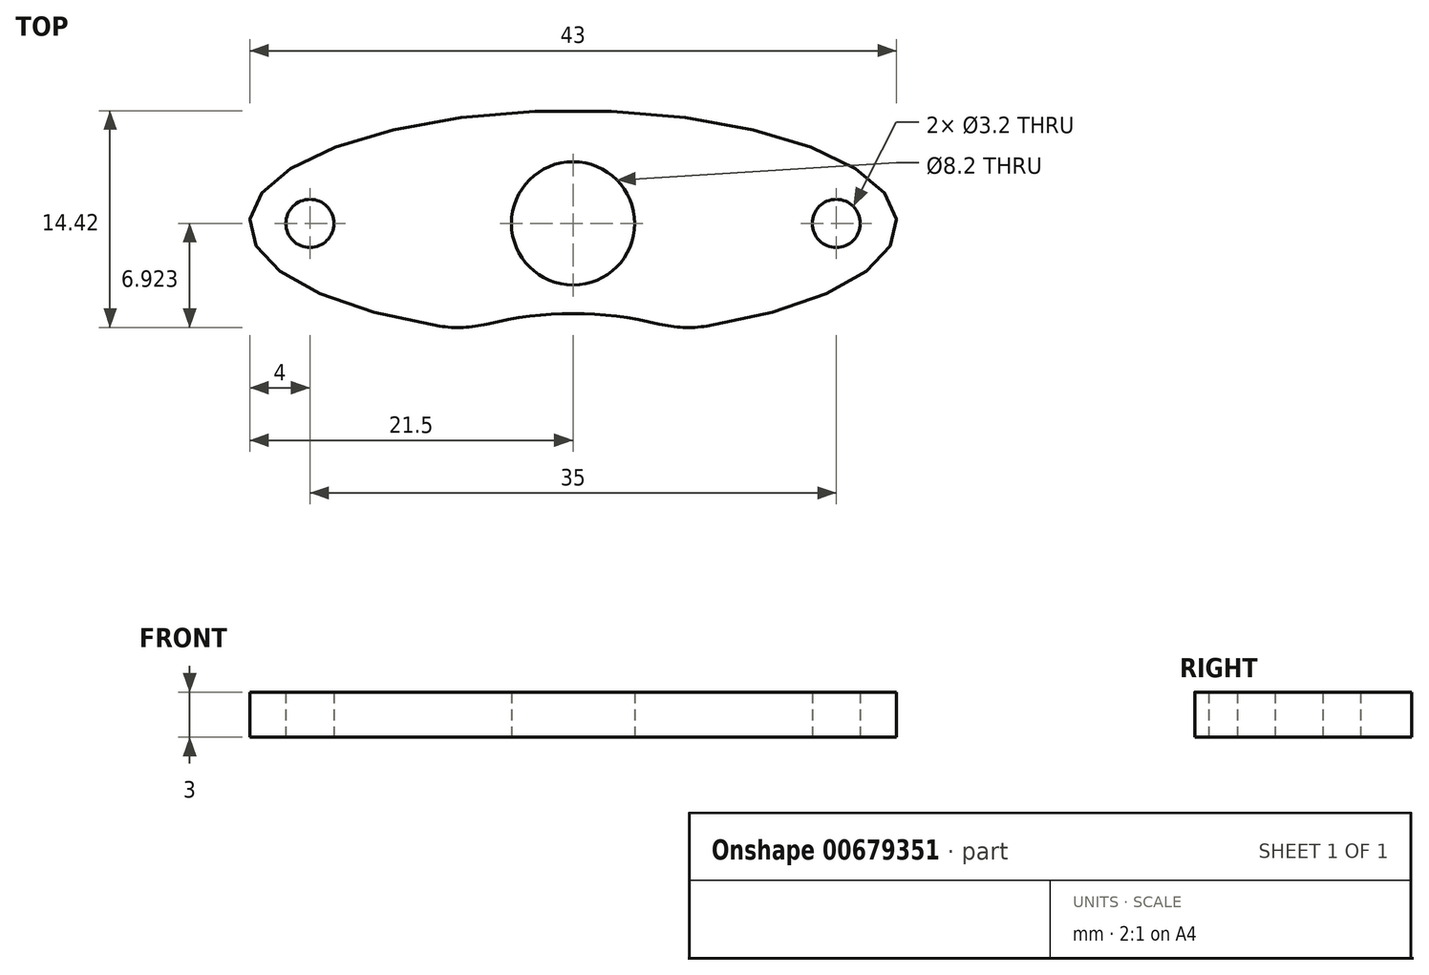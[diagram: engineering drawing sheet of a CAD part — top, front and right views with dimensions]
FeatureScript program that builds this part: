
annotation { "Feature Type Name" : "Feature", "Feature Type Description" : "" }
export const myFeature = defineFeature(function(context is Context, id is Id, definition is map)
    precondition{}
    {
        {
            var Q0;
            Q0=qCreatedBy(makeId("Top.planeOp"),FACE);
            var sketch = newSketch(context, id + "F0", { "sketchPlane" : qUnion([Q0])});
            skCircle(sketch, "E0", {"center": v(17.5, -0.29) * mm, "radius": 1.6 * mm});
            skArc(sketch, "E1", {"start": v(5.73, -6.98) * mm, "mid": v(0, -6.29) * mm, "end": v(-5.73, -6.98) * mm});
            skArc(sketch, "E2", {"start": v(5.73, -6.98) * mm, "mid": v(7.3, -7.2) * mm, "end": v(8.9, -7.11) * mm});
            skArc(sketch, "E3", {"start": v(-8.9, -7.11) * mm, "mid": v(-7.3, -7.2) * mm, "end": v(-5.73, -6.98) * mm});
            skCircle(sketch, "E4", {"center": v(-17.5, -0.29) * mm, "radius": 1.6 * mm});
            skEllipticalArc(sketch, "E5", {});
            skCircle(sketch, "E6", {"center": v(0, -0.29) * mm, "radius": 4.1 * mm});
            const initialGuessF0  = {"E5": [0, -0.00028677000000000005, -21.5, 0, 0.0215, 0.0075, 1.997442, 7.427336]};
            skSetInitialGuess(sketch, initialGuessF0);
            skSolve(sketch);
        }
        {
            var Q0;
            Q0 = qSketchRegion(id + "F0", true);
            extrude(context, id + "F1", {"entities" : qUnion([Q0]), "depth" : 3 * mm, "offsetDistance" : 25 * mm});
        }
    });
